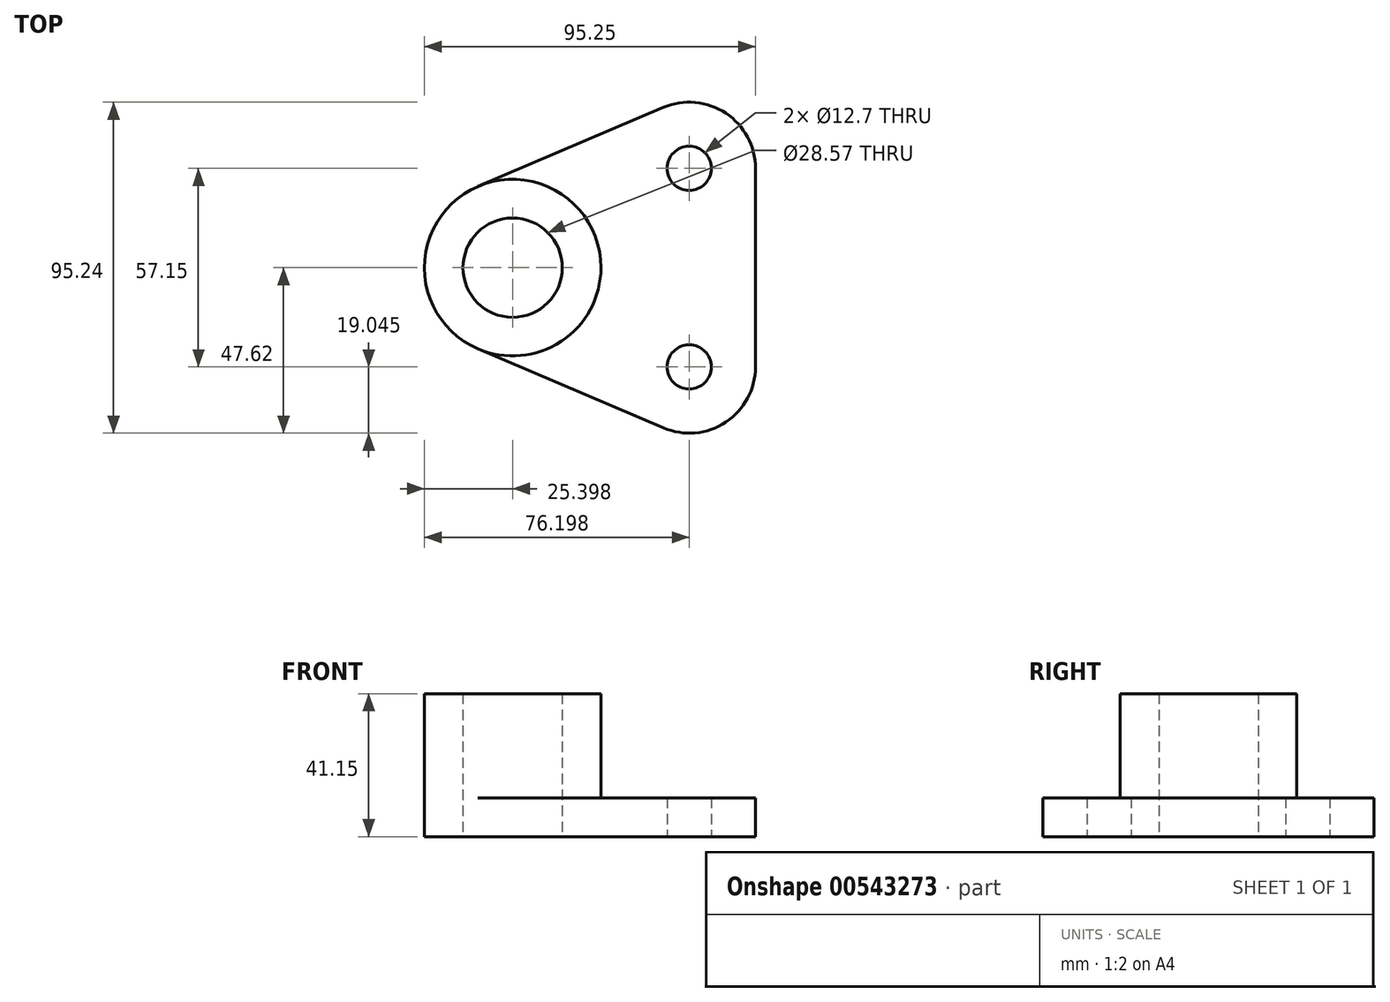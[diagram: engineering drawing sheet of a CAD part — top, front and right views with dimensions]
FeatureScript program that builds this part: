
annotation { "Feature Type Name" : "Feature", "Feature Type Description" : "" }
export const myFeature = defineFeature(function(context is Context, id is Id, definition is map)
    precondition{}
    {
        {
            var Q0;
            Q0=qCreatedBy(makeId("Top.planeOp"),FACE);
            var sketch = newSketch(context, id + "F0", { "sketchPlane" : qUnion([Q0])});
            skCircle(sketch, "E0", {"center": v(-51.43, 0) * mm, "radius": 25.4 * mm});
            skCircle(sketch, "E1", {"center": v(-51.43, 0) * mm, "radius": 14.29 * mm});
            skCircle(sketch, "E2", {"center": v(-0.63, 28.58) * mm, "radius": 19.05 * mm});
            skCircle(sketch, "E3", {"center": v(-0.63, -28.58) * mm, "radius": 19.05 * mm});
            skLineSegment(sketch, "E4", {"start": v(-61.4, 23.36) * mm, "end": v(-8.1, 46.1) * mm});
            skLineSegment(sketch, "E5", {"start": v(-61.4, -23.36) * mm, "end": v(-8.1, -46.1) * mm});
            skLineSegment(sketch, "E6", {"start": v(-51.43, 0) * mm, "end": v(46.34, 0) * mm, "construction": true});
            skCircle(sketch, "E7", {"center": v(-0.63, 28.58) * mm, "radius": 6.35 * mm});
            skCircle(sketch, "E8", {"center": v(-0.63, -28.58) * mm, "radius": 6.35 * mm});
            skLineSegment(sketch, "E9", {"start": v(18.42, 28.58) * mm, "end": v(18.42, -28.57) * mm});
            skSolve(sketch);
        }
        {
            var Q0;
            Q0=makeQuery(id+"F0.imprint","IMPRINT",FACE,{"disambiguationData":[TD([[makeQuery(id+"F0.imprint","IMPRINT",EDGE,{"derivedFrom":sQuery(id+"F0.wireOp",EDGE,"E7")}),-1.0]])]});
            var Q1;
            Q1=makeQuery(id+"F0.imprint","IMPRINT",FACE,{"disambiguationData":[TD([[makeQuery(id+"F0.imprint","IMPRINT",EDGE,{"derivedFrom":sQuery(id+"F0.wireOp",EDGE,"E8")}),1.0]])]});
            var Q2;
            Q2=makeQuery(id+"F0.imprint","IMPRINT",FACE,{"disambiguationData":[TD([[makeQuery(id+"F0.imprint","IMPRINT",EDGE,{"derivedFrom":sQuery(id+"F0.wireOp",EDGE,"E1")}),1.0]])]});
            var Q3;
            Q3=makeQuery(id+"F0.imprint","IMPRINT",FACE,{"disambiguationData":[TD([[makeQuery(id+"F0.imprint","IMPRINT",EDGE,{"derivedFrom":sQuery(id+"F0.wireOp",EDGE,"E7")}),1.0]])]});
            var Q4;
            Q4=makeQuery(id+"F0.imprint","IMPRINT",FACE,{"disambiguationData":[TD([[makeQuery(id+"F0.imprint","IMPRINT",EDGE,{"derivedFrom":sQuery(id+"F0.wireOp",EDGE,"E1")}),-1.0]])]});
            var Q5;
            Q5=makeQuery(id+"F0.imprint","IMPRINT",FACE,{"disambiguationData":[TD([[makeQuery(id+"F0.imprint","IMPRINT",EDGE,{"derivedFrom":sQuery(id+"F0.wireOp",EDGE,"E8")}),-1.0]])]});
            var Q6;
            {var subQ0=sQuery(id+"F0.wireOp",EDGE,"E4");Q6=makeQuery(id+"F0.imprint","IMPRINT",FACE,{"disambiguationData":[TD([[makeQuery(id+"F0.imprint","IMPRINT",EDGE,{"derivedFrom":subQ0}),-1.0]])]});}
            extrude(context, id + "F1", {"entities" : qUnion([Q0, Q1, Q2, Q3, Q4, Q5, Q6]), "depth" : 11.18 * mm, "offsetDistance" : 25.4 * mm});
        }
        {
            var Q0;
            Q0=makeQuery(id+"F0.imprint","IMPRINT",FACE,{"disambiguationData":[TD([[makeQuery(id+"F0.imprint","IMPRINT",EDGE,{"derivedFrom":sQuery(id+"F0.wireOp",EDGE,"E1")}),-1.0]])]});
            extrude(context, id + "F2", {"entities" : qUnion([Q0]), "operationType" : NewBodyOperationType.ADD, "depth" : 41.15 * mm, "offsetDistance" : 25.4 * mm});
        }
        {
            var Q0;
            Q0=makeQuery(id+"F2.boolean.opBoolean","SPLIT",FACE,{"disambiguationData":[TD([makeQuery(id+"F2.opExtrude","SWEPT_FACE",FACE,{"disambiguationData":[OSD([sQuery(id+"F0.wireOp",EDGE,"E1")])]})])],"derivedFrom":makeQuery(id+"F1.opExtrude","CAP_FACE",FACE,{"disambiguationData":[OSD([sQuery(id+"F0.wireOp",EDGE,"E0"),sQuery(id+"F0.wireOp",EDGE,"E2"),sQuery(id+"F0.wireOp",EDGE,"E3"),sQuery(id+"F0.wireOp",EDGE,"E4"),sQuery(id+"F0.wireOp",EDGE,"E5"),sQuery(id+"F0.wireOp",EDGE,"E9")])],"isStart":false})});
            extrude(context, id + "F3", {"entities" : qUnion([Q0]), "operationType" : NewBodyOperationType.REMOVE, "endBound" : BoundingType.THROUGH_ALL, "oppositeDirection" : true, "depth" : 25.4 * mm, "offsetDistance" : 25.4 * mm});
        }
        {
            var Q0;
            Q0=makeQuery(id+"F0.imprint","IMPRINT",FACE,{"disambiguationData":[TD([[makeQuery(id+"F0.imprint","IMPRINT",EDGE,{"derivedFrom":sQuery(id+"F0.wireOp",EDGE,"E7")}),1.0]])]});
            var Q1;
            Q1=makeQuery(id+"F0.imprint","IMPRINT",FACE,{"disambiguationData":[TD([[makeQuery(id+"F0.imprint","IMPRINT",EDGE,{"derivedFrom":sQuery(id+"F0.wireOp",EDGE,"E8")}),1.0]])]});
            extrude(context, id + "F4", {"entities" : qUnion([Q0, Q1]), "operationType" : NewBodyOperationType.REMOVE, "endBound" : BoundingType.THROUGH_ALL, "depth" : 25.4 * mm, "offsetDistance" : 25.4 * mm});
        }
    });
